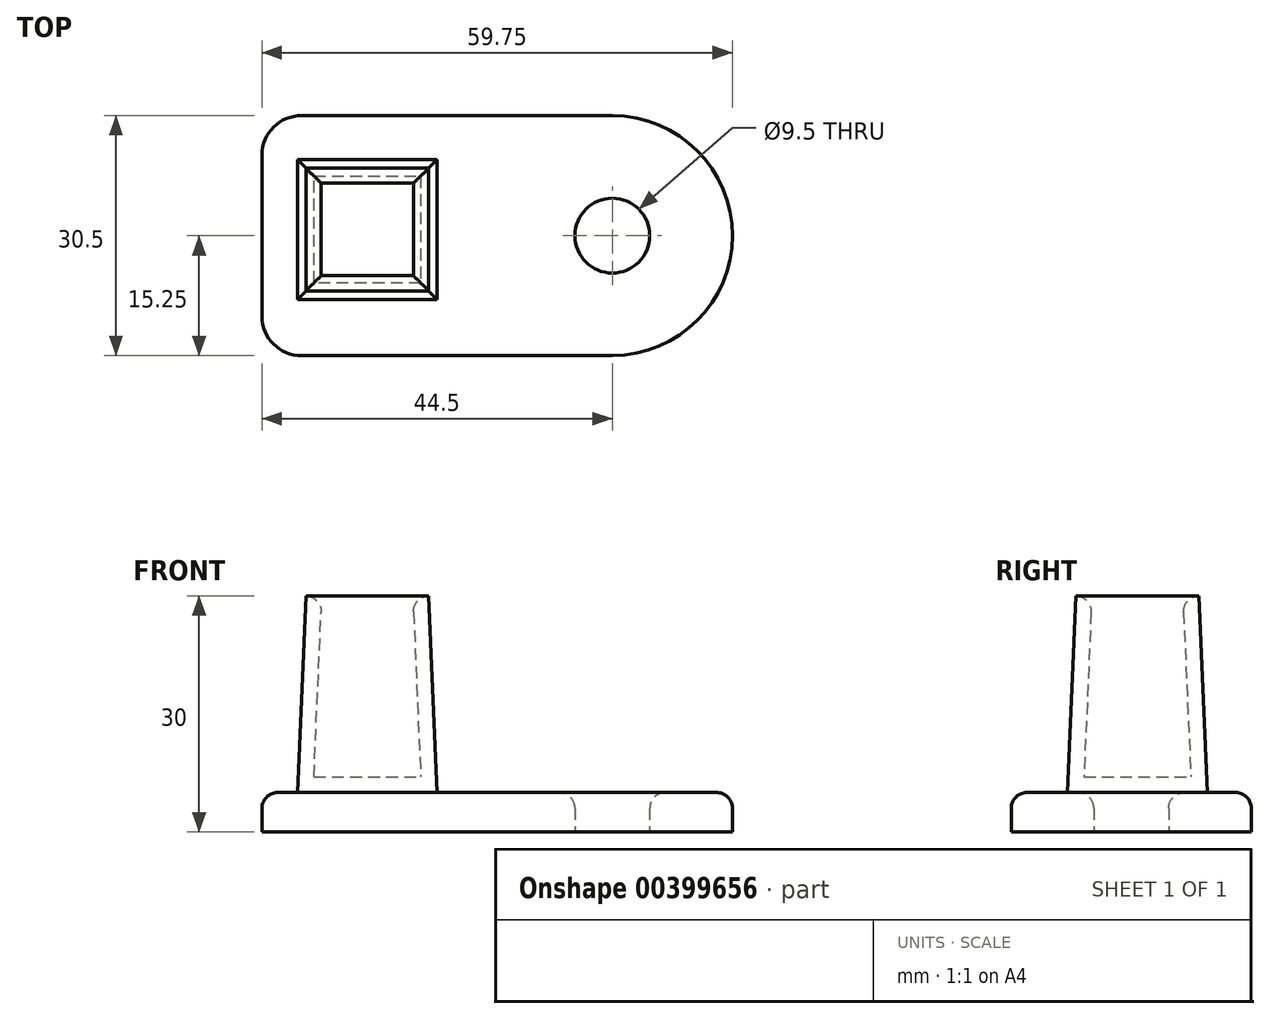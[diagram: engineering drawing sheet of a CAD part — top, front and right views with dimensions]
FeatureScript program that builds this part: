
annotation { "Feature Type Name" : "Feature", "Feature Type Description" : "" }
export const myFeature = defineFeature(function(context is Context, id is Id, definition is map)
    precondition{}
    {
        {
            var Q0;
            Q0=qCreatedBy(makeId("Top.planeOp"),FACE);
            var sketch = newSketch(context, id + "F0", { "sketchPlane" : qUnion([Q0])});
            skLineSegment(sketch, "E0.bottom", {"start": v(-22.25, 15.25) * mm, "end": v(22.25, 15.25) * mm});
            skLineSegment(sketch, "E0.top", {"start": v(-22.25, -15.25) * mm, "end": v(22.25, -15.25) * mm});
            skLineSegment(sketch, "E0.left", {"start": v(-22.25, 15.25) * mm, "end": v(-22.25, -15.25) * mm});
            skLineSegment(sketch, "E0.right", {"start": v(22.25, 15.25) * mm, "end": v(22.25, -15.25) * mm, "construction": true});
            skPoint(sketch, "E0.middle", {"position": v(0, 0) * mm});
            skCircle(sketch, "E1", {"center": v(22.25, 0) * mm, "radius": 4.75 * mm});
            skCircle(sketch, "E2", {"center": v(22.25, 0) * mm, "radius": 15.25 * mm});
            skSolve(sketch);
        }
        {
            var Q0;
            {var subQ0=sQuery(id+"F0.wireOp",EDGE,"E0.bottom");Q0=makeQuery(id+"F0.imprint","IMPRINT",FACE,{"disambiguationData":[TD([[makeQuery(id+"F0.imprint","IMPRINT",EDGE,{"derivedFrom":subQ0}),-1.0]])]});}
            var Q1;
            Q1=makeQuery(id+"F0.imprint","IMPRINT",FACE,{"disambiguationData":[TD([[makeQuery(id+"F0.imprint","IMPRINT",EDGE,{"derivedFrom":sQuery(id+"F0.wireOp",EDGE,"E1")}),-1.0]])]});
            extrude(context, id + "F1", {"entities" : qUnion([Q0, Q1]), "depth" : 5 * mm});
        }
        {
            var Q0;
            Q0=makeQuery(id+"F1.opExtrude","CAP_FACE",FACE,{"disambiguationData":[OSD([sQuery(id+"F0.wireOp",EDGE,"E0.bottom"),sQuery(id+"F0.wireOp",EDGE,"E0.top"),sQuery(id+"F0.wireOp",EDGE,"E0.left"),sQuery(id+"F0.wireOp",EDGE,"E1"),sQuery(id+"F0.wireOp",EDGE,"E2")])],"isStart":false});
            var sketch = newSketch(context, id + "F2", { "sketchPlane" : qUnion([Q0])});
            skLineSegment(sketch, "E3.bottom", {"start": v(-17.75, 9.65) * mm, "end": v(0, 9.65) * mm});
            skLineSegment(sketch, "E3.top", {"start": v(-17.75, -8.1) * mm, "end": v(0, -8.1) * mm});
            skLineSegment(sketch, "E3.left", {"start": v(-17.75, 9.65) * mm, "end": v(-17.75, -8.1) * mm});
            skLineSegment(sketch, "E3.right", {"start": v(0, 9.65) * mm, "end": v(0, -8.1) * mm});
            skSolve(sketch);
        }
        {
            var Q0;
            Q0=makeQuery(id+"F2.imprint","IMPRINT",FACE,{"disambiguationData":[TD([[makeQuery(id+"F2.imprint","IMPRINT",EDGE,{"derivedFrom":sQuery(id+"F2.wireOp",EDGE,"E3.bottom")}),-1.0]])]});
            extrude(context, id + "F3", {"entities" : qUnion([Q0]), "depth" : 25 * mm, "hasDraft" : true, "draftAngle" : 2.5 * degree, "draftPullDirection" : true});
        }
        {
            var Q0;
            Q0=makeQuery(id+"F3.opExtrude","CAP_FACE",FACE,{"disambiguationData":[OSD([sQuery(id+"F2.wireOp",EDGE,"E3.bottom"),sQuery(id+"F2.wireOp",EDGE,"E3.top"),sQuery(id+"F2.wireOp",EDGE,"E3.left"),sQuery(id+"F2.wireOp",EDGE,"E3.right")])],"isStart":false});
            shell(context, id + "F4", {"entities" : qUnion([Q0]), "thickness" : 2 * mm});
        }
        {
            var Q0;
            Q0=makeQuery(id+"F1.opExtrude","SWEPT_EDGE",EDGE,{"disambiguationData":[OSD([sQuery(id+"F0.wireOp",EDGE,"E0.top"),sQuery(id+"F0.wireOp",EDGE,"E0.left")])]});
            var Q1;
            Q1=makeQuery(id+"F1.opExtrude","SWEPT_EDGE",EDGE,{"disambiguationData":[OSD([sQuery(id+"F0.wireOp",EDGE,"E0.bottom"),sQuery(id+"F0.wireOp",EDGE,"E0.left")])]});
            fillet(context, id + "F5", {"entities" : qUnion([Q0, Q1]), "radius" : 5 * mm, "tangentPropagation" : true, "allowEdgeOverflow" : false});
        }
        {
            var Q0;
            Q0=makeQuery(id+"F1.opExtrude","CAP_FACE",FACE,{"disambiguationData":[OSD([sQuery(id+"F0.wireOp",EDGE,"E0.bottom"),sQuery(id+"F0.wireOp",EDGE,"E0.top"),sQuery(id+"F0.wireOp",EDGE,"E0.left"),sQuery(id+"F0.wireOp",EDGE,"E1"),sQuery(id+"F0.wireOp",EDGE,"E2")])],"isStart":false});
            var Q1;
            {var subQ0=sQuery(id+"F2.wireOp",EDGE,"E3.bottom");Q1=makeQuery(id+"F4.opShell","OFFSET_EDGE",EDGE,{"disambiguationData":[OSD([subQ0]),TDD([makeQuery(id+"F3.opExtrude","CAP_EDGE",EDGE,{"disambiguationData":[OSD([subQ0])],"isStart":false})])]});}
            var Q2;
            {var subQ0=sQuery(id+"F2.wireOp",EDGE,"E3.left");Q2=makeQuery(id+"F4.opShell","OFFSET_EDGE",EDGE,{"disambiguationData":[OSD([subQ0]),TDD([makeQuery(id+"F3.opExtrude","CAP_EDGE",EDGE,{"disambiguationData":[OSD([subQ0])],"isStart":false})])]});}
            var Q3;
            {var subQ0=sQuery(id+"F2.wireOp",EDGE,"E3.top");Q3=makeQuery(id+"F4.opShell","OFFSET_EDGE",EDGE,{"disambiguationData":[OSD([subQ0]),TDD([makeQuery(id+"F3.opExtrude","CAP_EDGE",EDGE,{"disambiguationData":[OSD([subQ0])],"isStart":false})])]});}
            var Q4;
            {var subQ0=sQuery(id+"F2.wireOp",EDGE,"E3.right");Q4=makeQuery(id+"F4.opShell","OFFSET_EDGE",EDGE,{"disambiguationData":[OSD([subQ0]),TDD([makeQuery(id+"F3.opExtrude","CAP_EDGE",EDGE,{"disambiguationData":[OSD([subQ0])],"isStart":false})])]});}
            fillet(context, id + "F6", {"entities" : qUnion([Q0, Q1, Q2, Q3, Q4]), "radius" : 2 * mm, "tangentPropagation" : true, "allowEdgeOverflow" : false});
        }
    });
